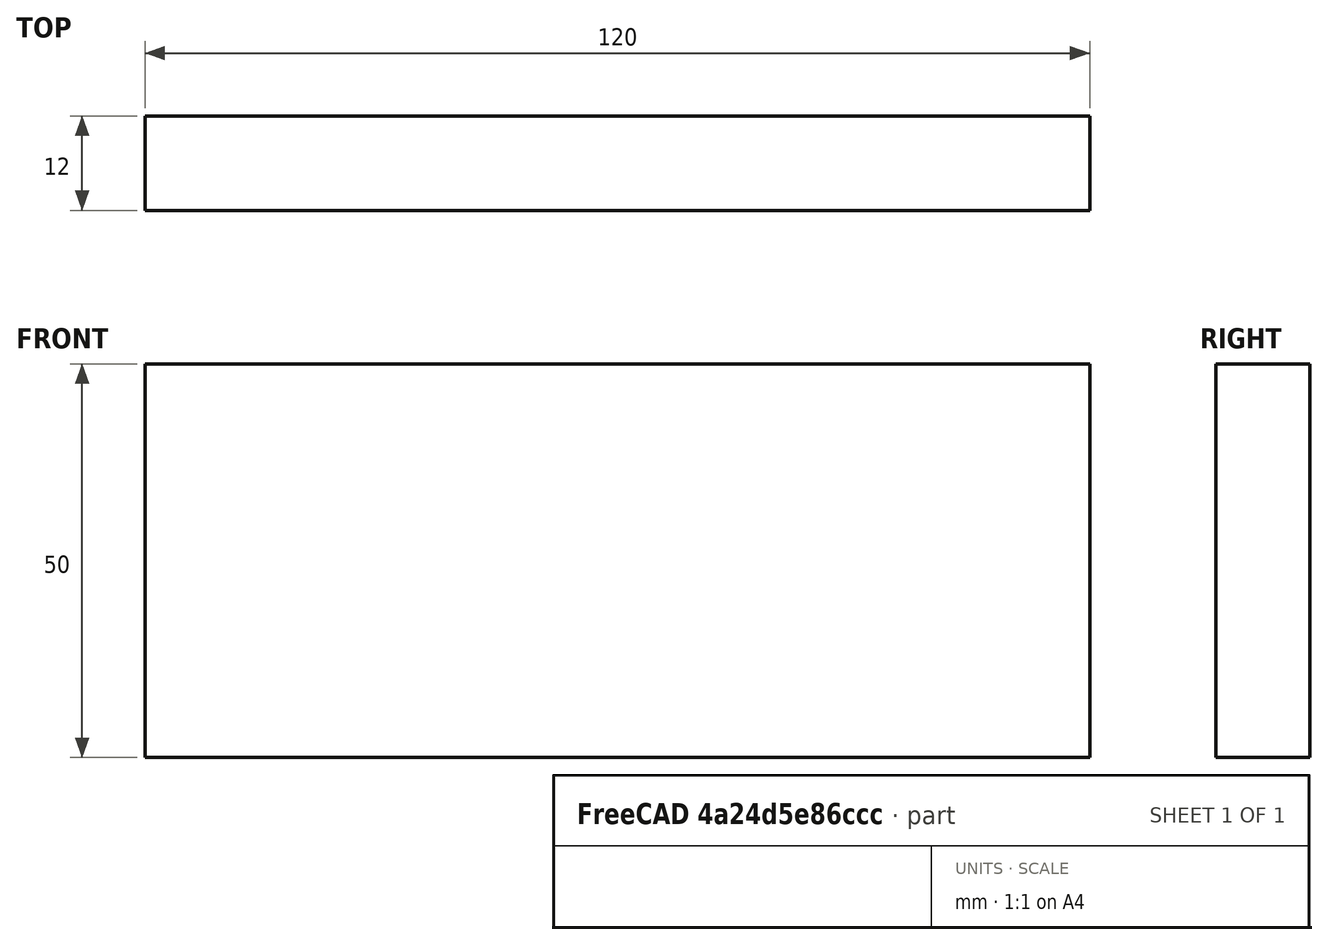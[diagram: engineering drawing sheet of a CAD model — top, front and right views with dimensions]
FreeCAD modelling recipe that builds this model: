
FCSTD DOCUMENT  (FreeCAD 0.15R4671 (Git))
Label: Flat Bar 120x12 EN10058 S235JR
License: All rights reserved
LicenseURL: http://en.wikipedia.org/wiki/All_rights_reserved
objects: Sketcher::SketchObject×1, Part::Extrusion×1
note: 2 computed .brp shape members not serialized (recipe doc carries the construction recipe); baked Part::Feature solids carry a one-line shape summary decoded from their .brp

FEATURE [Sketcher::SketchObject] Sketch
  sketch-geometry (4):
    g0: LineSegment StartX=-60 StartY=-6 StartZ=0 EndX=60 EndY=-6 EndZ=0
    g1: LineSegment StartX=60 StartY=-6 StartZ=0 EndX=60 EndY=6 EndZ=0
    g2: LineSegment StartX=60 StartY=6 StartZ=0 EndX=-60 EndY=6 EndZ=0
    g3: LineSegment StartX=-60 StartY=6 StartZ=0 EndX=-60 EndY=-6 EndZ=0
  constraints (12):
    c: Coincident(g0,g1)
    c: Coincident(g1,g2)
    c: Coincident(g2,g3)
    c: Coincident(g3,g0)
    c: Horizontal(g0)
    c: Horizontal(g2)
    c: Vertical(g1)
    c: Vertical(g3)
    c: Symmetric(g1,g2,g-2)
    c: Symmetric(g0,g1,g-1)
    c: DistanceY(g1) = 12
    c: DistanceX(g0) = 120
FEATURE [Part::Extrusion] Extrude  label="Flat Bar 120x12 EN10058 S235JR"
  Base = -> Sketch
  Dir = (0,0,50)
  Solid = true
